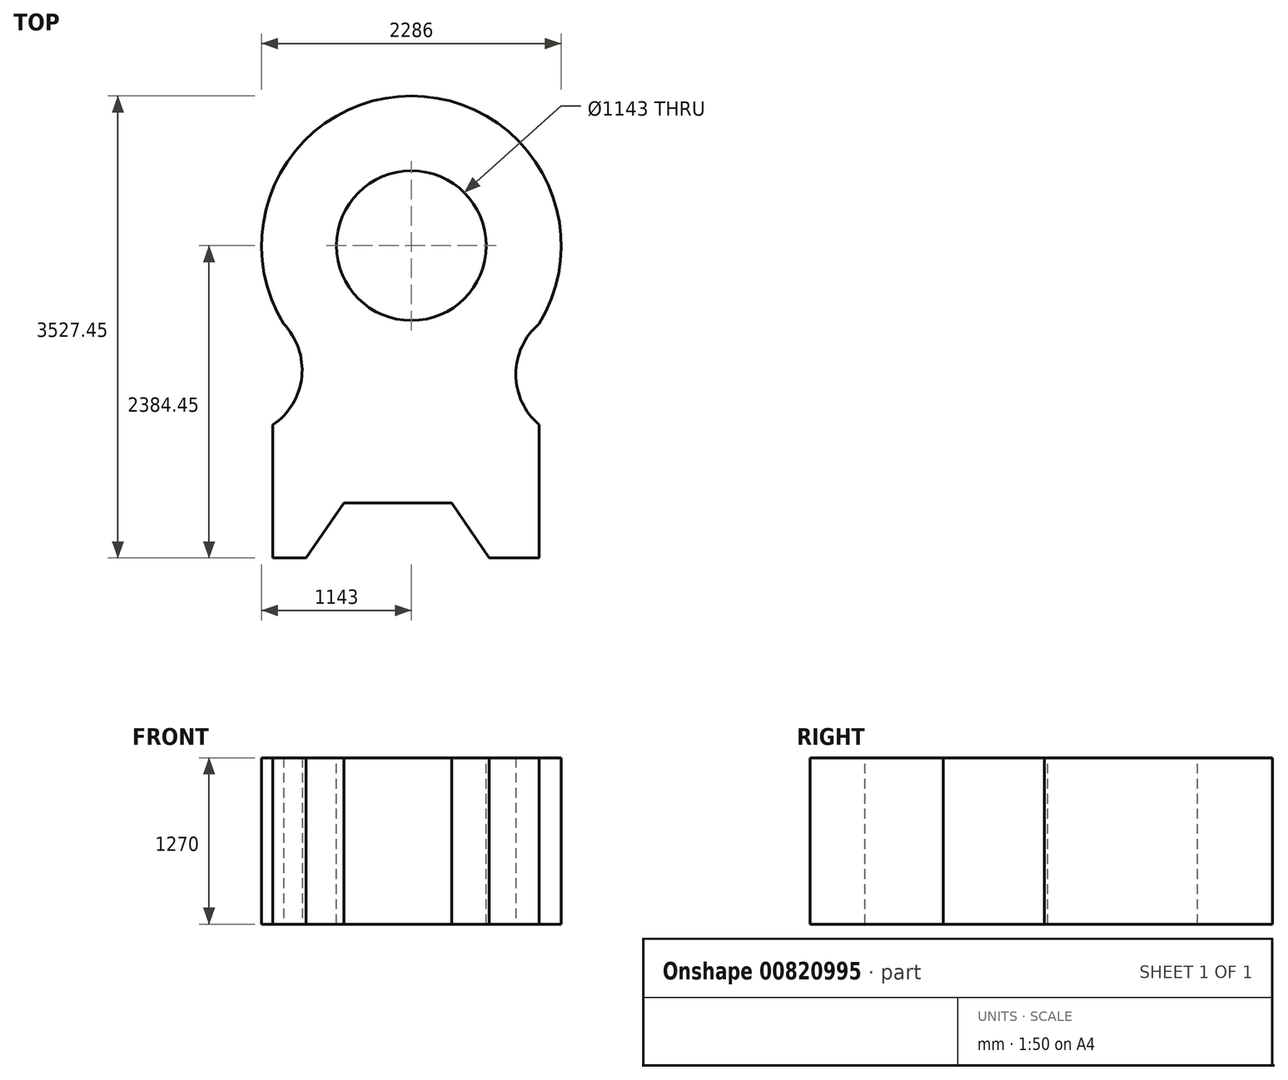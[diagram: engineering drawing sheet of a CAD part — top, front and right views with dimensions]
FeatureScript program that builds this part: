
annotation { "Feature Type Name" : "Feature", "Feature Type Description" : "" }
export const myFeature = defineFeature(function(context is Context, id is Id, definition is map)
    precondition{}
    {
        {
            var Q0;
            Q0=qCreatedBy(makeId("Top.planeOp"),FACE);
            var sketch = newSketch(context, id + "F0", { "sketchPlane" : qUnion([Q0])});
            skLineSegment(sketch, "E0", {"start": v(0, 0) * mm, "end": v(0, 1016) * mm});
            skLineSegment(sketch, "E1", {"start": v(0, 0) * mm, "end": v(254, 0) * mm});
            skLineSegment(sketch, "E2", {"start": v(254, 0) * mm, "end": v(2032, 0) * mm});
            skLineSegment(sketch, "E3", {"start": v(2032, 0) * mm, "end": v(2032, 1016) * mm});
            skArc(sketch, "E4", {"start": v(0, 1016) * mm, "mid": v(220.2, 1383.58) * mm, "end": v(80.94, 1788.8) * mm});
            skArc(sketch, "E5", {"start": v(2032, 1788.8) * mm, "mid": v(1853.78, 1402.4) * mm, "end": v(2032, 1016) * mm});
            skArc(sketch, "E6", {"start": v(2032, 1788.8) * mm, "mid": v(1056.47, 3527.45) * mm, "end": v(80.94, 1788.8) * mm});
            skSolve(sketch);
        }
        {
            var Q0;
            Q0 = qSketchRegion(id + "F0", true);
            extrude(context, id + "F1", {"entities" : qUnion([Q0]), "depth" : 1270 * mm, "offsetDistance" : 25.4 * mm});
        }
        {
            var Q0;
            Q0=makeQuery(id+"F1.opExtrude","CAP_FACE",FACE,{"disambiguationData":[OSD([sQuery(id+"F0.wireOp",EDGE,"E0"),sQuery(id+"F0.wireOp",EDGE,"E1"),sQuery(id+"F0.wireOp",EDGE,"E2"),sQuery(id+"F0.wireOp",EDGE,"E3"),sQuery(id+"F0.wireOp",EDGE,"E4"),sQuery(id+"F0.wireOp",EDGE,"E5"),sQuery(id+"F0.wireOp",EDGE,"E6")])],"isStart":false});
            var sketch = newSketch(context, id + "F2", { "sketchPlane" : qUnion([Q0])});
            skCircle(sketch, "E7", {"center": v(1056.47, 2384.45) * mm, "radius": 571.5 * mm});
            skLineSegment(sketch, "E8", {"start": v(0, 0) * mm, "end": v(254, 0) * mm});
            skLineSegment(sketch, "E9", {"start": v(254, 0) * mm, "end": v(540.71, 419.36) * mm});
            skLineSegment(sketch, "E10", {"start": v(540.71, 419.36) * mm, "end": v(1362.93, 419.36) * mm});
            skLineSegment(sketch, "E11", {"start": v(1362.93, 419.36) * mm, "end": v(1649.64, 0) * mm});
            skSolve(sketch);
        }
        {
            var Q0;
            {var subQ0=sQuery(id+"F2.wireOp",EDGE,"E9");Q0=makeQuery(id+"F2.imprint","IMPRINT",FACE,{"disambiguationData":[TD([[makeQuery(id+"F2.imprint","IMPRINT",EDGE,{"derivedFrom":subQ0}),-1.0]])]});}
            var Q1;
            Q1=makeQuery(id+"F2.imprint","IMPRINT",FACE,{"disambiguationData":[TD([[makeQuery(id+"F2.imprint","IMPRINT",EDGE,{"derivedFrom":sQuery(id+"F2.wireOp",EDGE,"E7")}),1.0]])]});
            extrude(context, id + "F3", {"entities" : qUnion([Q0, Q1]), "operationType" : NewBodyOperationType.REMOVE, "endBound" : BoundingType.THROUGH_ALL, "oppositeDirection" : true, "depth" : 25.4 * mm, "offsetDistance" : 25.4 * mm});
        }
    });
